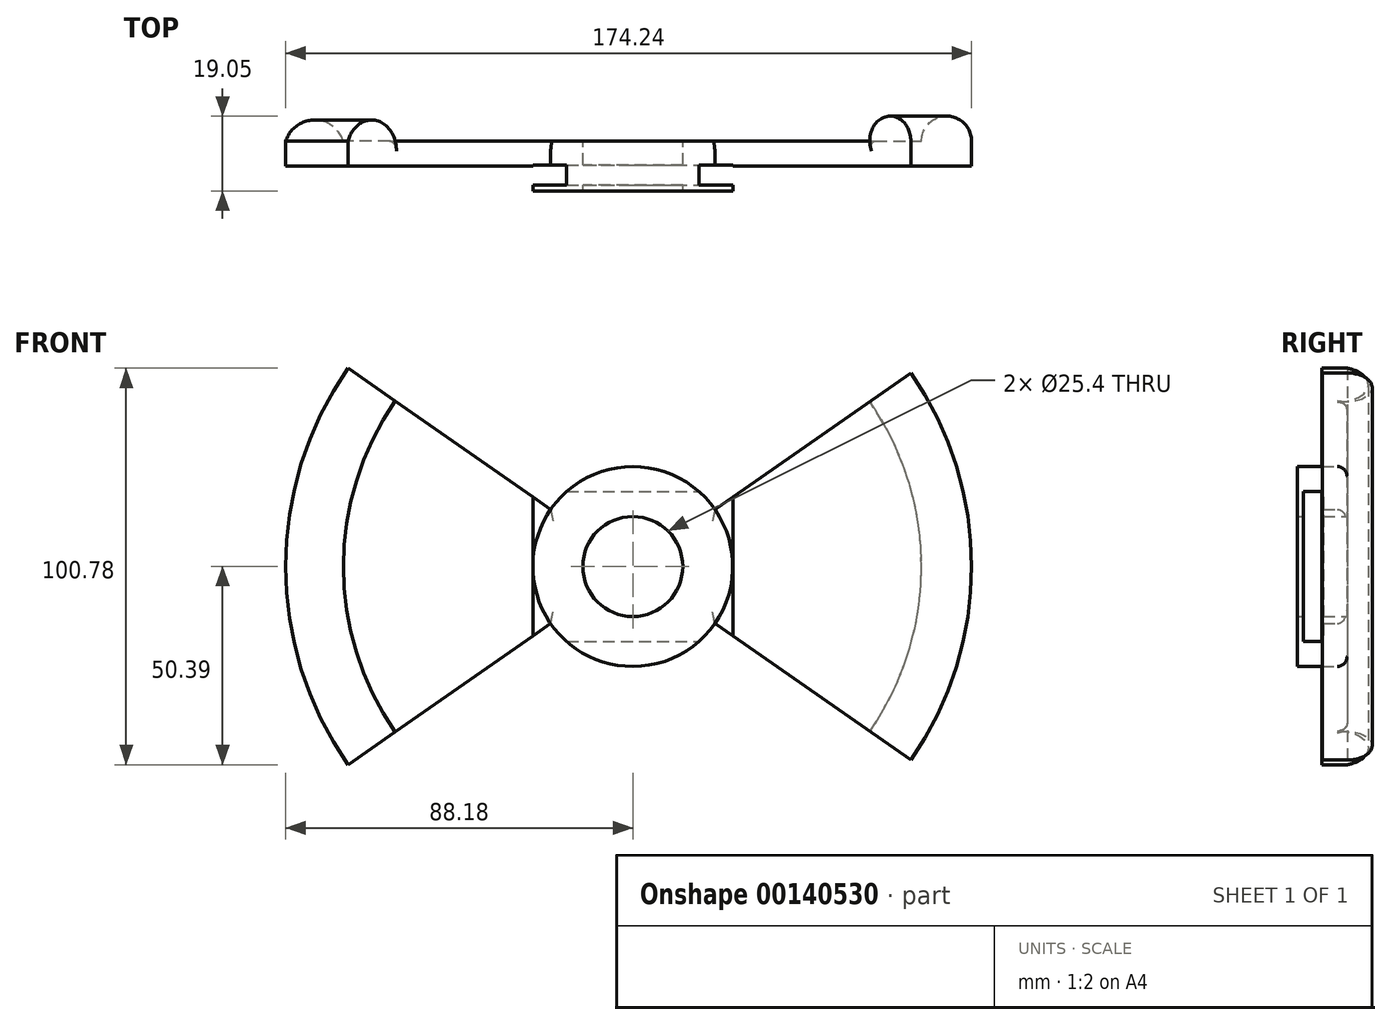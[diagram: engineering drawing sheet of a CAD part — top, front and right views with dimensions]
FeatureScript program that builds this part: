
annotation { "Feature Type Name" : "Feature", "Feature Type Description" : "" }
export const myFeature = defineFeature(function(context is Context, id is Id, definition is map)
    precondition{}
    {
        {
            var Q0;
            Q0=qCreatedBy(makeId("Front.planeOp"),FACE);
            var sketch = newSketch(context, id + "F0", { "sketchPlane" : qUnion([Q0])});
            skCircle(sketch, "E0", {"center": v(0, 0) * mm, "radius": 25.4 * mm});
            skLineSegment(sketch, "E1", {"start": v(-72.96, 50.8) * mm, "end": v(0, 0) * mm});
            skLineSegment(sketch, "E2", {"start": v(0, 0) * mm, "end": v(72.96, -50.8) * mm});
            skLineSegment(sketch, "E3", {"start": v(0, 0) * mm, "end": v(72.96, 50.8) * mm});
            skLineSegment(sketch, "E4", {"start": v(0, 0) * mm, "end": v(-72.96, -50.8) * mm});
            skCircle(sketch, "E5", {"center": v(0, 0) * mm, "radius": 12.7 * mm});
            skArc(sketch, "E6", {"start": v(-72.96, 50.8) * mm, "mid": v(-92.36, 0) * mm, "end": v(-72.96, -50.8) * mm});
            skArc(sketch, "E7", {"start": v(72.96, -50.8) * mm, "mid": v(92.36, 0) * mm, "end": v(72.96, 50.8) * mm});
            skLineSegment(sketch, "E8", {"start": v(-72.96, 50.8) * mm, "end": v(-62.53, 43.54) * mm});
            skLineSegment(sketch, "E9", {"start": v(72.96, 50.8) * mm, "end": v(62.53, 43.54) * mm});
            skArc(sketch, "E10", {"start": v(62.53, -43.54) * mm, "mid": v(76.2, 0) * mm, "end": v(62.53, 43.54) * mm});
            skArc(sketch, "E11", {"start": v(-62.53, 43.54) * mm, "mid": v(-76.2, 0) * mm, "end": v(-62.53, -43.54) * mm});
            skSolve(sketch);
        }
        {
            var Q0;
            {var subQ5=sQuery(id+"F0.wireOp",EDGE,"E11");Q0=makeQuery(id+"F0.imprint","IMPRINT",FACE,{"disambiguationData":[TD([[makeQuery(id+"F0.imprint","IMPRINT",EDGE,{"derivedFrom":subQ5}),1.0]])]});}
            var Q1;
            {var subQ5=sQuery(id+"F0.wireOp",EDGE,"E10");Q1=makeQuery(id+"F0.imprint","IMPRINT",FACE,{"disambiguationData":[TD([[makeQuery(id+"F0.imprint","IMPRINT",EDGE,{"derivedFrom":subQ5}),1.0]])]});}
            extrude(context, id + "F1", {"entities" : qUnion([Q0, Q1]), "depth" : 6.35 * mm});
        }
        {
            var Q0;
            {var subQ0=sQuery(id+"F0.wireOp",EDGE,"E1");var subQ1=sQuery(id+"F0.wireOp",EDGE,"E0");var subQ2=makeQuery(id+"F0.imprint","INTERSECT",VERTEX,{"derivedFrom":[subQ1,subQ0]});Q0=makeQuery(id+"F0.imprint","IMPRINT",FACE,{"disambiguationData":[TD([[makeQuery(id+"F0.imprint","IMPRINT",EDGE,{"disambiguationData":[TD([[subQ2,1.0]])],"derivedFrom":subQ1}),1.0]])]});}
            var Q1;
            {var subQ0=sQuery(id+"F0.wireOp",EDGE,"E1");var subQ1=sQuery(id+"F0.wireOp",EDGE,"E0");var subQ2=makeQuery(id+"F0.imprint","INTERSECT",VERTEX,{"derivedFrom":[subQ1,subQ0]});Q1=makeQuery(id+"F0.imprint","IMPRINT",FACE,{"disambiguationData":[TD([[makeQuery(id+"F0.imprint","IMPRINT",EDGE,{"disambiguationData":[TD([[subQ2,-1.0]])],"derivedFrom":subQ1}),1.0]])]});}
            var Q2;
            {var subQ0=sQuery(id+"F0.wireOp",EDGE,"E4");var subQ1=sQuery(id+"F0.wireOp",EDGE,"E0");var subQ2=makeQuery(id+"F0.imprint","INTERSECT",VERTEX,{"derivedFrom":[subQ1,subQ0]});Q2=makeQuery(id+"F0.imprint","IMPRINT",FACE,{"disambiguationData":[TD([[makeQuery(id+"F0.imprint","IMPRINT",EDGE,{"disambiguationData":[TD([[subQ2,-1.0]])],"derivedFrom":subQ1}),1.0]])]});}
            var Q3;
            {var subQ0=sQuery(id+"F0.wireOp",EDGE,"E3");var subQ1=sQuery(id+"F0.wireOp",EDGE,"E0");var subQ2=makeQuery(id+"F0.imprint","INTERSECT",VERTEX,{"derivedFrom":[subQ1,subQ0]});Q3=makeQuery(id+"F0.imprint","IMPRINT",FACE,{"disambiguationData":[TD([[makeQuery(id+"F0.imprint","IMPRINT",EDGE,{"disambiguationData":[TD([[subQ2,1.0]])],"derivedFrom":subQ1}),1.0]])]});}
            extrude(context, id + "F2", {"entities" : qUnion([Q0, Q1, Q2, Q3]), "depth" : 12.7 * mm});
        }
        {
            var Q0;
            Q0=sQuery(id+"F0.wireOp",VERTEX,"E8.start");
            var Q1;
            Q1=sQuery(id+"F0.wireOp",VERTEX,"E11.start");
            var Q2;
            Q2=makeQuery(id+"F1.opExtrude","CAP_VERTEX",VERTEX,{"disambiguationData":[OSD([sQuery(id+"F0.wireOp",EDGE,"E1"),sQuery(id+"F0.wireOp",EDGE,"E8"),sQuery(id+"F0.wireOp",EDGE,"E11")])],"isStart":false});
            cPlane(context, id + "F3", {"entities" : qUnion([Q0, Q1, Q2]), "cplaneType" : CPlaneType.THREE_POINT, "offset" : 25.4 * mm, "width" : 152.4 * mm, "height" : 152.4 * mm});
        }
        {
            var Q0;
            Q0=qCreatedBy(id+"F3.planeOp",FACE);
            var sketch = newSketch(context, id + "F4", { "sketchPlane" : qUnion([Q0])});
            skLineSegment(sketch, "E12", {"start": v(-73.53, -6.38) * mm, "end": v(-88.18, -6.38) * mm});
            skLineSegment(sketch, "E13", {"start": v(-88.18, 0) * mm, "end": v(-88.18, -6.38) * mm});
            skArc(sketch, "E14", {"start": v(-73.53, 0) * mm, "mid": v(-80.85, 5.35) * mm, "end": v(-88.18, 0) * mm});
            skLineSegment(sketch, "E15", {"start": v(-73.53, 0) * mm, "end": v(-73.53, -6.38) * mm});
            skSolve(sketch);
        }
        {
            var Q0;
            Q0=qSketchRegion(id+"F4",true);
            var Q1;
            Q1=sQuery(id+"F0.wireOp",EDGE,"E11");
            sweep(context, id + "F5", {"profiles" : qUnion([Q0]), "path" : qUnion([Q1])});
        }
        {
            var Q0;
            Q0=sQuery(id+"F0.wireOp",VERTEX,"E7.end");
            var Q1;
            Q1=sQuery(id+"F0.wireOp",VERTEX,"E9.end");
            var Q2;
            Q2=makeQuery(id+"F1.opExtrude","CAP_VERTEX",VERTEX,{"disambiguationData":[OSD([sQuery(id+"F0.wireOp",EDGE,"E3"),sQuery(id+"F0.wireOp",EDGE,"E9"),sQuery(id+"F0.wireOp",EDGE,"E10")])],"isStart":false});
            cPlane(context, id + "F6", {"entities" : qUnion([Q0, Q1, Q2]), "cplaneType" : CPlaneType.THREE_POINT, "offset" : 25.4 * mm, "width" : 152.4 * mm, "height" : 152.4 * mm});
        }
        {
            var Q0;
            Q0=qCreatedBy(id+"F6.planeOp",FACE);
            var sketch = newSketch(context, id + "F7", { "sketchPlane" : qUnion([Q0])});
            skLineSegment(sketch, "E16", {"start": v(86.06, 0) * mm, "end": v(73.36, 0) * mm});
            skLineSegment(sketch, "E17", {"start": v(73.36, 0) * mm, "end": v(73.36, 6.35) * mm});
            skLineSegment(sketch, "E18", {"start": v(73.36, 6.35) * mm, "end": v(86.06, 6.35) * mm});
            skLineSegment(sketch, "E19", {"start": v(86.06, 6.35) * mm, "end": v(86.06, 0) * mm});
            skArc(sketch, "E20", {"start": v(73.36, 0) * mm, "mid": v(79.7, -6.35) * mm, "end": v(86.06, 0) * mm});
            skSolve(sketch);
        }
        {
            var Q0;
            Q0=makeQuery(id+"F7.imprint","IMPRINT",FACE,{"disambiguationData":[TD([[makeQuery(id+"F7.imprint","IMPRINT",EDGE,{"derivedFrom":sQuery(id+"F7.wireOp",EDGE,"E16")}),-1.0]])]});
            var Q1;
            Q1=makeQuery(id+"F7.imprint","IMPRINT",FACE,{"disambiguationData":[TD([[makeQuery(id+"F7.imprint","IMPRINT",EDGE,{"derivedFrom":sQuery(id+"F7.wireOp",EDGE,"E16")}),1.0]])]});
            var Q2;
            Q2=makeQuery(id+"F1.opExtrude","CAP_EDGE",EDGE,{"disambiguationData":[OSD([sQuery(id+"F0.wireOp",EDGE,"E10")])],"isStart":false});
            sweep(context, id + "F8", {"profiles" : qUnion([Q0, Q1]), "path" : qUnion([Q2])});
        }
        {
            var Q0;
            Q0=qCreatedBy(makeId("Right.planeOp"),FACE);
            var sketch = newSketch(context, id + "F9", { "sketchPlane" : qUnion([Q0])});
            skLineSegment(sketch, "E21.bottom", {"start": v(-11.17, 19.05) * mm, "end": v(-6.1, 19.05) * mm});
            skLineSegment(sketch, "E21.top", {"start": v(-11.17, -19.05) * mm, "end": v(-6.1, -19.05) * mm});
            skLineSegment(sketch, "E21.left", {"start": v(-11.17, 19.05) * mm, "end": v(-11.17, -19.05) * mm});
            skLineSegment(sketch, "E21.right", {"start": v(-6.1, 19.05) * mm, "end": v(-6.1, -19.05) * mm});
            skSolve(sketch);
        }
        {
            var Q0;
            Q0=makeQuery(id+"F1.opExtrude","SWEPT_BODY",BODY,{"disambiguationData":[OSD([sQuery(id+"F0.wireOp",EDGE,"E0"),sQuery(id+"F0.wireOp",EDGE,"E1"),sQuery(id+"F0.wireOp",EDGE,"E4"),sQuery(id+"F0.wireOp",EDGE,"E11")])]});
            var Q1;
            Q1=makeQuery(id+"F1.opExtrude","SWEPT_BODY",BODY,{"disambiguationData":[OSD([sQuery(id+"F0.wireOp",EDGE,"E0"),sQuery(id+"F0.wireOp",EDGE,"E2"),sQuery(id+"F0.wireOp",EDGE,"E3"),sQuery(id+"F0.wireOp",EDGE,"E10")])]});
            var Q2;
            Q2=makeQuery(id+"F2.opExtrude","SWEPT_BODY",BODY,{"disambiguationData":[OSD([sQuery(id+"F0.wireOp",EDGE,"E0"),sQuery(id+"F0.wireOp",EDGE,"E5")])]});
            var Q3;
            Q3=makeQuery(id+"F5.opSweep","SWEPT_BODY",BODY,{"disambiguationData":[OSD([sQuery(id+"F0.wireOp",EDGE,"E11"),sQuery(id+"F4.wireOp",EDGE,"E12"),sQuery(id+"F4.wireOp",EDGE,"E13"),sQuery(id+"F4.wireOp",EDGE,"E14"),sQuery(id+"F4.wireOp",EDGE,"E15")])]});
            var Q4;
            Q4=makeQuery(id+"F8.opSweep","SWEPT_BODY",BODY,{"disambiguationData":[OSD([sQuery(id+"F0.wireOp",EDGE,"E10"),sQuery(id+"F7.wireOp",EDGE,"E17"),sQuery(id+"F7.wireOp",EDGE,"E18"),sQuery(id+"F7.wireOp",EDGE,"E19"),sQuery(id+"F7.wireOp",EDGE,"E20")])]});
            booleanBodies(context, id + "F10", {"operationType" : BooleanOperationType.UNION, "tools" : qUnion([Q0, Q1, Q2, Q3, Q4])});
        }
        {
            var Q0;
            Q0 = qSketchRegion(id + "F9", true);
            extrude(context, id + "F11", {"entities" : qUnion([Q0]), "operationType" : NewBodyOperationType.REMOVE, "oppositeDirection" : true, "depth" : 25.4 * mm, "hasSecondDirection" : true, "secondDirectionOppositeDirection" : false, "secondDirectionDepth" : 25.4 * mm});
        }
        {
            var Q0;
            Q0=makeQuery(id+"F1.opExtrude","CAP_EDGE",EDGE,{"disambiguationData":[OSD([sQuery(id+"F0.wireOp",EDGE,"E3")])],"isStart":true});
            var Q1;
            Q1=makeQuery(id+"F1.opExtrude","CAP_EDGE",EDGE,{"disambiguationData":[OSD([sQuery(id+"F0.wireOp",EDGE,"E2")])],"isStart":true});
            var Q2;
            {var subQ1=sQuery(id+"F0.wireOp",EDGE,"E2");var subQ3=sQuery(id+"F0.wireOp",EDGE,"E0");Q2=makeQuery(id+"F10.opBoolean","SPLIT",EDGE,{"disambiguationData":[TD([makeQuery(id+"F1.opExtrude","SWEPT_FACE",FACE,{"disambiguationData":[OSD([subQ1])]})])],"derivedFrom":makeQuery(id+"F2.opExtrude","CAP_EDGE",EDGE,{"disambiguationData":[OSD([subQ3])],"isStart":true})});}
            var Q3;
            Q3=makeQuery(id+"F1.opExtrude","CAP_EDGE",EDGE,{"disambiguationData":[OSD([sQuery(id+"F0.wireOp",EDGE,"E4")])],"isStart":true});
            var Q4;
            Q4=makeQuery(id+"F1.opExtrude","CAP_EDGE",EDGE,{"disambiguationData":[OSD([sQuery(id+"F0.wireOp",EDGE,"E1")])],"isStart":true});
            var Q5;
            {var subQ1=sQuery(id+"F0.wireOp",EDGE,"E1");var subQ2=sQuery(id+"F0.wireOp",EDGE,"E0");Q5=makeQuery(id+"F10.opBoolean","SPLIT",EDGE,{"disambiguationData":[TD([makeQuery(id+"F1.opExtrude","SWEPT_FACE",FACE,{"disambiguationData":[OSD([subQ1])]})])],"derivedFrom":makeQuery(id+"F2.opExtrude","CAP_EDGE",EDGE,{"disambiguationData":[OSD([subQ2])],"isStart":true})});}
            fillet(context, id + "F12", {"entities" : qUnion([Q0, Q1, Q2, Q3, Q4, Q5]), "radius" : 2.54 * mm, "tangentPropagation" : true, "allowEdgeOverflow" : false});
        }
    });
